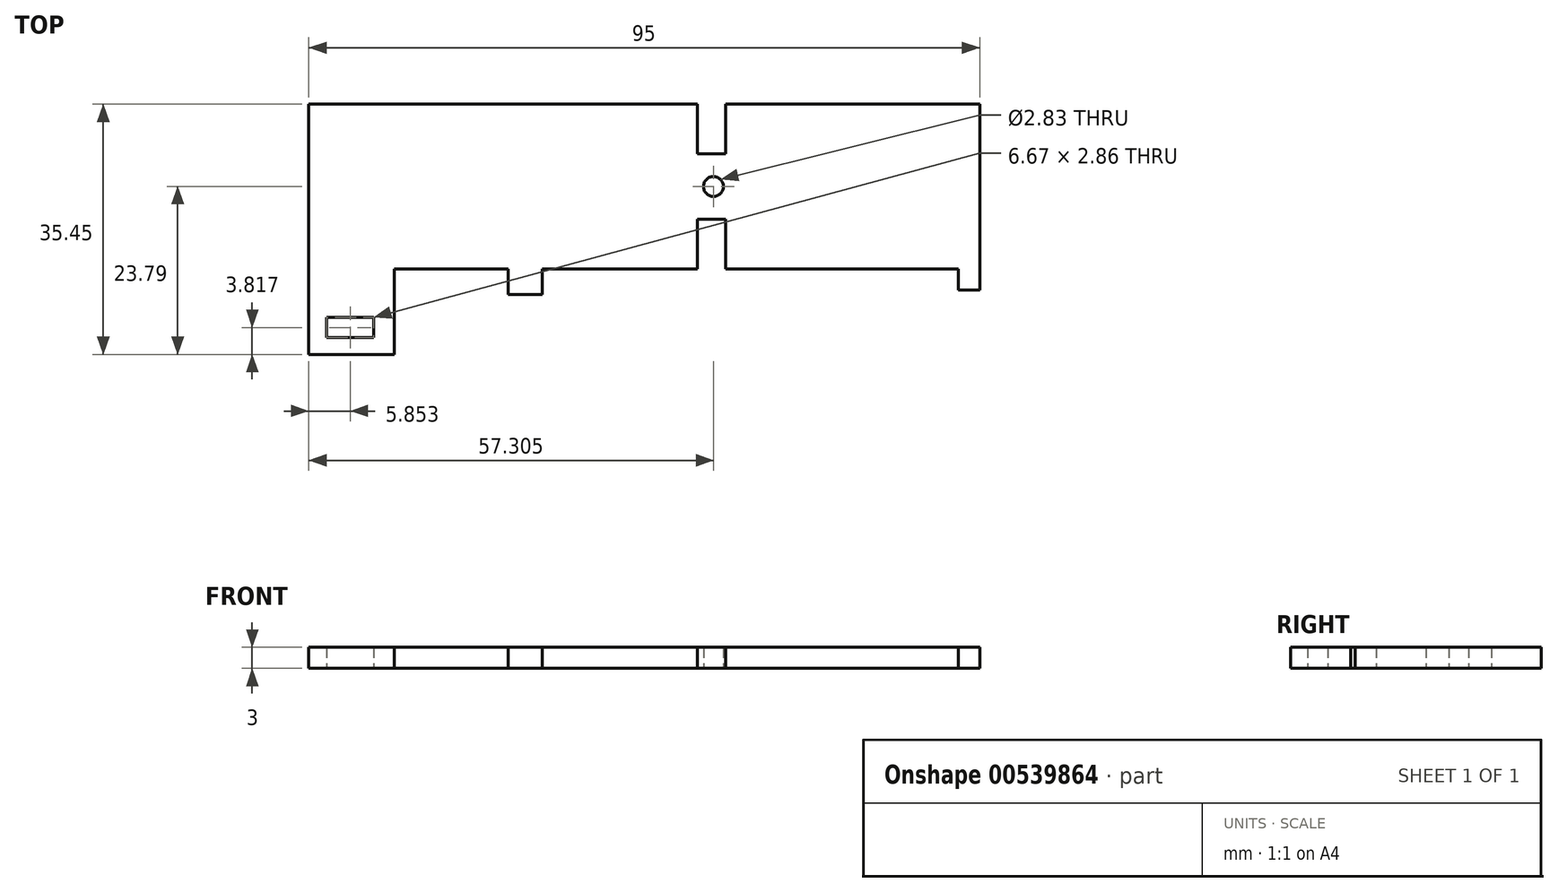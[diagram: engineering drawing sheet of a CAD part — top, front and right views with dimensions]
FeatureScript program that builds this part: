
annotation { "Feature Type Name" : "Feature", "Feature Type Description" : "" }
export const myFeature = defineFeature(function(context is Context, id is Id, definition is map)
    precondition{}
    {
        {
            var Q0;
            Q0=qCreatedBy(makeId("Top.planeOp"),FACE);
            var sketch = newSketch(context, id + "F0", { "sketchPlane" : qUnion([Q0])});
            skLineSegment(sketch, "E0.bottom", {"start": v(-47.5, 11.66) * mm, "end": v(7.5, 11.66) * mm});
            skLineSegment(sketch, "E0.top", {"start": v(-35.4, -11.66) * mm, "end": v(-19.26, -11.66) * mm});
            skLineSegment(sketch, "E0.left", {"start": v(-47.5, 11.66) * mm, "end": v(-47.5, -11.66) * mm});
            skLineSegment(sketch, "E0.right", {"start": v(47.5, 11.66) * mm, "end": v(47.5, -11.66) * mm});
            skPoint(sketch, "E0.middle", {"position": v(0, 0) * mm});
            skLineSegment(sketch, "E1.top", {"start": v(-47.5, -23.8) * mm, "end": v(-35.4, -23.8) * mm});
            skLineSegment(sketch, "E1.left", {"start": v(-47.5, -11.66) * mm, "end": v(-47.5, -23.8) * mm});
            skLineSegment(sketch, "E1.right", {"start": v(-35.4, -11.66) * mm, "end": v(-35.4, -23.8) * mm});
            skLineSegment(sketch, "E2.top", {"start": v(-19.26, -15.3) * mm, "end": v(-14.45, -15.3) * mm});
            skLineSegment(sketch, "E2.left", {"start": v(-19.26, -11.66) * mm, "end": v(-19.26, -15.3) * mm});
            skLineSegment(sketch, "E2.right", {"start": v(-14.45, -11.66) * mm, "end": v(-14.45, -15.3) * mm});
            skLineSegment(sketch, "E3.trimOffspring", {"start": v(-14.45, -11.66) * mm, "end": v(7.5, -11.66) * mm});
            skPoint(sketch, "E4", {"position": v(9.5, -8.16) * mm});
            skPoint(sketch, "E5", {"position": v(9.5, 8.16) * mm});
            skLineSegment(sketch, "E6.bottom", {"start": v(7.5, 4.66) * mm, "end": v(11.5, 4.66) * mm});
            skLineSegment(sketch, "E6.left", {"start": v(7.5, 4.66) * mm, "end": v(7.5, 11.66) * mm});
            skLineSegment(sketch, "E6.right", {"start": v(11.5, 4.66) * mm, "end": v(11.5, 11.66) * mm});
            skLineSegment(sketch, "E7.bottom", {"start": v(11.5, -4.66) * mm, "end": v(7.5, -4.66) * mm});
            skLineSegment(sketch, "E7.left", {"start": v(11.5, -4.66) * mm, "end": v(11.5, -11.66) * mm});
            skLineSegment(sketch, "E7.right", {"start": v(7.5, -4.66) * mm, "end": v(7.5, -11.66) * mm});
            skLineSegment(sketch, "E8.trimOffspring", {"start": v(11.5, 11.66) * mm, "end": v(47.5, 11.66) * mm});
            skLineSegment(sketch, "E9.trimOffspring", {"start": v(11.5, -11.66) * mm, "end": v(44.5, -11.66) * mm});
            skLineSegment(sketch, "E10.top", {"start": v(47.5, -14.66) * mm, "end": v(44.5, -14.66) * mm});
            skLineSegment(sketch, "E10.left", {"start": v(47.5, -11.66) * mm, "end": v(47.5, -14.66) * mm});
            skLineSegment(sketch, "E10.right", {"start": v(44.5, -11.66) * mm, "end": v(44.5, -14.66) * mm});
            skSolve(sketch);
        }
        {
            var Q0;
            Q0=makeQuery(id+"F0.imprint","IMPRINT",FACE,{"disambiguationData":[TD([[makeQuery(id+"F0.imprint","IMPRINT",EDGE,{"derivedFrom":sQuery(id+"F0.wireOp",EDGE,"E0.bottom")}),-1.0]])]});
            extrude(context, id + "F1", {"entities" : qUnion([Q0]), "depth" : 3 * mm, "offsetDistance" : 25 * mm});
        }
        {
            var Q0;
            Q0=makeQuery(id+"F1.opExtrude","CAP_FACE",FACE,{"disambiguationData":[OSD([sQuery(id+"F0.wireOp",EDGE,"E0.bottom"),sQuery(id+"F0.wireOp",EDGE,"E0.top"),sQuery(id+"F0.wireOp",EDGE,"E0.left"),sQuery(id+"F0.wireOp",EDGE,"E0.right"),sQuery(id+"F0.wireOp",EDGE,"E1.top"),sQuery(id+"F0.wireOp",EDGE,"E1.left"),sQuery(id+"F0.wireOp",EDGE,"E1.right"),sQuery(id+"F0.wireOp",EDGE,"E2.top"),sQuery(id+"F0.wireOp",EDGE,"E2.left"),sQuery(id+"F0.wireOp",EDGE,"E2.right"),sQuery(id+"F0.wireOp",EDGE,"E3.trimOffspring"),sQuery(id+"F0.wireOp",EDGE,"E6.bottom"),sQuery(id+"F0.wireOp",EDGE,"E6.left"),sQuery(id+"F0.wireOp",EDGE,"E6.right"),sQuery(id+"F0.wireOp",EDGE,"E7.bottom"),sQuery(id+"F0.wireOp",EDGE,"E7.left"),sQuery(id+"F0.wireOp",EDGE,"E7.right"),sQuery(id+"F0.wireOp",EDGE,"E8.trimOffspring"),sQuery(id+"F0.wireOp",EDGE,"E9.trimOffspring"),sQuery(id+"F0.wireOp",EDGE,"E10.top"),sQuery(id+"F0.wireOp",EDGE,"E10.left"),sQuery(id+"F0.wireOp",EDGE,"E10.right")])],"isStart":true});
            var sketch = newSketch(context, id + "F2", { "sketchPlane" : qUnion([Q0])});
            skCircle(sketch, "E11", {"center": v(9.8, 0) * mm, "radius": 1.41 * mm});
            skLineSegment(sketch, "E12.bottom", {"start": v(-44.98, 21.4) * mm, "end": v(-38.31, 21.4) * mm});
            skLineSegment(sketch, "E12.top", {"start": v(-44.98, 18.54) * mm, "end": v(-38.31, 18.54) * mm});
            skLineSegment(sketch, "E12.left", {"start": v(-44.98, 21.4) * mm, "end": v(-44.98, 18.54) * mm});
            skLineSegment(sketch, "E12.right", {"start": v(-38.31, 21.4) * mm, "end": v(-38.31, 18.54) * mm});
            skSolve(sketch);
        }
        {
            var Q0;
            Q0=makeQuery(id+"F2.imprint","IMPRINT",FACE,{"disambiguationData":[TD([[makeQuery(id+"F2.imprint","IMPRINT",EDGE,{"derivedFrom":sQuery(id+"F2.wireOp",EDGE,"E12.bottom")}),-1.0]])]});
            var Q1;
            Q1=makeQuery(id+"F2.imprint","IMPRINT",FACE,{"disambiguationData":[TD([[makeQuery(id+"F2.imprint","IMPRINT",EDGE,{"derivedFrom":sQuery(id+"F2.wireOp",EDGE,"E11")}),1.0]])]});
            extrude(context, id + "F3", {"entities" : qUnion([Q0, Q1]), "operationType" : NewBodyOperationType.REMOVE, "oppositeDirection" : true, "depth" : 25 * mm, "offsetDistance" : 25 * mm});
        }
    });
